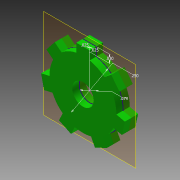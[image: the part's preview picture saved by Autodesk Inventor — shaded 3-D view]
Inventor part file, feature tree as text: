
AUTODESK INVENTOR PART (.ipt)
format: ipt  version: 2015 (Build 190159000, 159)  size: 131,072 bytes
history: native  units: in
note: dims shown in document units (in); Inventor stores cm internally (conversion verified against a paired STEP export)
features: extrude x2, sketch x1, pattern_circular x1
ambient origin geometry x8: Origin, YZ Plane, XZ Plane, XY Plane, X Axis, Y Axis, Z Axis, Center Point
bodies: Solid1 (feature_tree)
feature tree (4):
  sketch  "Sketch1"  dims[d0=0.03in d2=0.025in d3=0.025in d4=0.25in d5=0.079in d6=0.05in d7=0.0in d8=0.05in d9=0.0in d10=2.7559in d11=360.0deg]
  extrude  "Extrusion1"  Depth=0.025in
  extrude  "Extrusion2"  Depth=0.025in
  pattern_circular  "Circular Pattern1"  [2 undecoded]
note: 2 required parameter values undecoded (feature->parameter linkage not recoverable at this tier; creation-order binding heuristic only, values carry confidence <= 0.55)
